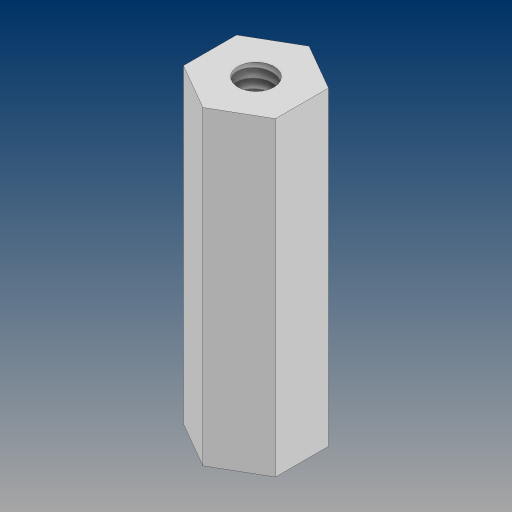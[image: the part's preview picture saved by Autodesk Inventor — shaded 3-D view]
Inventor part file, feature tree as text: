
AUTODESK INVENTOR PART (.ipt)
format: ipt  version: 2024.3 (Build 283343000, 343)  size: 93,696 bytes
history: native  units: in
note: dims shown in document units (in); Inventor stores cm internally (conversion verified against a paired STEP export)
features: sketch x2, extrude x1, hole x1
ambient origin geometry x8: Origin, YZ Plane, XZ Plane, XY Plane, X Axis, Y Axis, Z Axis, Center Point
bodies: Solid1 (feature_tree)
feature tree (4):
  extrude  "Extrusion1"  Depth=1.688in TaperAngle=0.0deg
  hole  "Hole1"  [1 undecoded]
  sketch  "Sketch1"  dims[d0=0.5in d1=1.688in d2=0.0in]
  sketch  "Sketch2"  dims[d3=0.196in d4=1.0in d5=0.375in d6=0.25in d7=0.5635in d8=1.0in d9=0.8108in]
note: 1 required parameter value undecoded (feature->parameter linkage not recoverable at this tier; creation-order binding heuristic only, values carry confidence <= 0.55)
